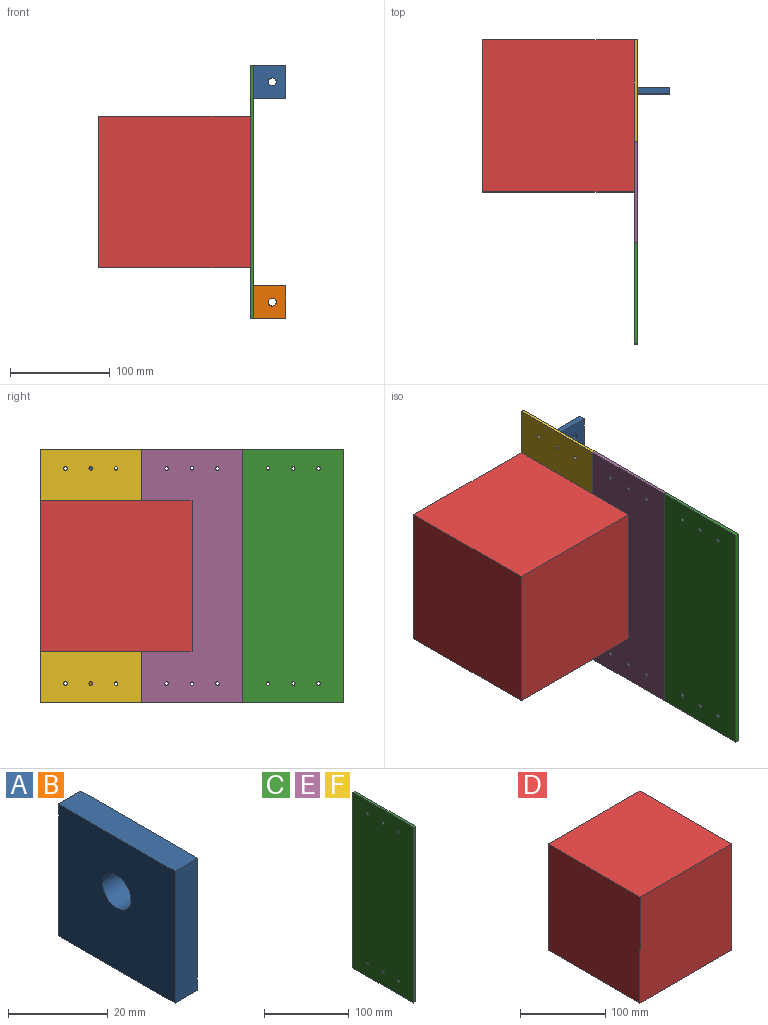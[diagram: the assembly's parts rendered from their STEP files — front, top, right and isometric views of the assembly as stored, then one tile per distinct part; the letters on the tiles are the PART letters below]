
ASSEMBLY  parts=6 mates=8
PART A: 7 faces, bbox 6.4x33x32.4 mm
  f0: plane 32.39x6.35mm, normal (0,-1,0), area 205.6mm2, adj f1,f3,f5,f6
  f1: plane 33.02x6.35mm, normal (0,0,-1), area 209.7mm2, adj f0,f2,f5,f6
  f2: plane 32.39x6.35mm, normal (0,1,0), area 205.6mm2, adj f1,f3,f5,f6
  f3: plane 33.02x6.35mm, normal (0,0,1), area 209.7mm2, adj f0,f2,f5,f6
  f4: cylinder r=4mm len=8mm, axis (-1,0,0), area 159.6mm2, adj f5,f6
  f5: plane 33.02x32.39mm, normal (1,0,0), area 1019.1mm2, adj f0,f1,f2,f3,f4
  f6: plane 33.02x32.39mm, normal (-1,0,0), area 1019.1mm2, adj f0,f1,f2,f3,f4
PART B: same geometry as A
PART C: 12 faces, bbox 3.2x101.6x254 mm
  f0: plane 254x3.18mm, normal (0,-1,0), area 806.5mm2, adj f1,f8,f10,f11
  f1: plane 101.6x3.18mm, normal (0,0,-1), area 322.6mm2, adj f0,f2,f10,f11
  f2: plane 254x3.18mm, normal (0,1,0), area 806.5mm2, adj f1,f8,f10,f11
  f3: cylinder r=1.79mm len=3.57mm, axis (-1,0,0), area 35.6mm2, adj f10,f11
  f4: cylinder r=1.79mm len=3.57mm, axis (-1,0,0), area 35.6mm2, adj f10,f11
  f5: cylinder r=1.79mm len=3.57mm, axis (-1,0,0), area 35.6mm2, adj f10,f11
  f6: cylinder r=1.79mm len=3.57mm, axis (-1,0,0), area 35.6mm2, adj f10,f11
  f7: cylinder r=1.79mm len=3.57mm, axis (-1,0,0), area 35.6mm2, adj f10,f11
  f8: plane 101.6x3.18mm, normal (0,0,1), area 322.6mm2, adj f0,f2,f10,f11
  f9: cylinder r=1.79mm len=3.57mm, axis (-1,0,0), area 35.6mm2, adj f10,f11
  f10: plane 254x101.6mm, normal (1,0,0), area 25746.3mm2, adj f0,f1,f2,f3,f4,f5,f6,f7
  f11: plane 254x101.6mm, normal (-1,0,0), area 25746.3mm2, adj f0,f1,f2,f3,f4,f5,f6,f7
PART D: 6 faces, bbox 152.4x152.4x152.4 mm
  f0: plane 152.4x152.4mm, normal (0,-1,0), area 23225.8mm2, adj f1,f3,f4,f5
  f1: plane 152.4x152.4mm, normal (0,0,-1), area 23225.8mm2, adj f0,f2,f4,f5
  f2: plane 152.4x152.4mm, normal (0,1,0), area 23225.8mm2, adj f1,f3,f4,f5
  f3: plane 152.4x152.4mm, normal (0,0,1), area 23225.8mm2, adj f0,f2,f4,f5
  f4: plane 152.4x152.4mm, normal (1,0,0), area 23225.8mm2, adj f0,f1,f2,f3
  f5: plane 152.4x152.4mm, normal (-1,0,0), area 23225.8mm2, adj f0,f1,f2,f3
PART E: same geometry as C
PART F: same geometry as C
PLACE A rot(axis=(-0.58,0.58,-0.58),120deg) t=(-43.03,59.99,250.86)mm
PLACE B rot(axis=(0.58,0.58,0.58),120deg) t=(-43.03,53.64,-3.14)mm
PLACE C rot(axis=(1,0,0),180deg) t=(-46.2,-95.58,250.86)mm
PLACE D rot(axis=(0.71,0,0.71),180deg) t=(-198.6,107.62,47.66)mm
PLACE E rot(axis=(1,0,0),180deg) t=(-46.2,6.02,250.86)mm
PLACE F t=(-46.2,6.02,-3.14)mm
MATE planar C.f0 <-> E.f2  axis (0,1,0) through (-44.61,-95.58,123.86)mm
MATE planar A.f1 <-> F.f10  axis (-1,0,0) through (-43.03,56.82,234.35)mm
MATE planar B.f0 <-> F.f1  axis (0,0,-1) through (-10.64,56.82,-3.14)mm
MATE planar D.f0 <-> F.f2  axis (0,1,0) through (-122.4,107.62,123.86)mm
MATE planar A.f0 <-> F.f8  axis (0,0,1) through (-26.83,56.82,250.86)mm
MATE planar B.f1 <-> F.f10  axis (-1,0,0) through (-43.03,56.82,-3.14)mm
MATE planar E.f0 <-> F.f0  axis (0,1,0) through (-44.61,6.02,123.86)mm
MATE planar D.f3 <-> F.f11  axis (1,0,0) through (-46.2,31.42,123.86)mm
